# Revit family: Firestop-Joint_Sealant_ES_Elastomeric_Sealant_Floor_to_Floor
name_source: partatom
category: Specialty Equipment
units: mm (PartAtom-declared; Revit-internal decimal feet)

## family parameters
Classification Number = 23.20.50.11
Cut with Voids When Loaded = No
Enable Cutting in Views = No
Maintain Annotation Orientation = No
Part Type = Normal
Room Calculation Point = No
Round Connector Dimension = Use Diameter
Shared = No

## types (4) — shared parameters
Assembly Code = D4030900
Color = Pale Blue or Red
Default Elevation = 0' - 0"
Description = SpecSeal® ES Silicone Firestop Sealant
Elastomeric Firestop Joint Sealant = Firestop-STI-ES-Elastomeric Joint Sealant
Fire Rating = Up to 4 Hr
Guide Specification = http://www.stifirestop.com
LEED Information = http://files.systems.stifirestop.com
Locate Distributor = http://www.stifirestop.com
MSDS = http://files.systems.stifirestop.com
Manufacturer = Specified Technologies Inc.
Manufacturer Fax No. = 908.526.9623
Model = Series ES Sealant
Product Documentation Link = http://files.systems.stifirestop.com
Product Page URL = http://www.stifirestop.com
Sealant Thickness = 0' - 0 1/8"
Tested Systems = http://systems.stifirestop.com
URL = http://www.stifirestop.com

## per-type parameters (varying)
| type | Floor to Floor Gap |
| 1"-Gap | 0' - 1" |
| 2"-Gap | 0' - 2" |
| 3"-Gap | 0' - 3" |
| 4"-Gap | 0' - 4" |

## geometry (parser evidence)
native form markers: Blend x12, Sweep x2
no freeform markers — native parametric forms only
